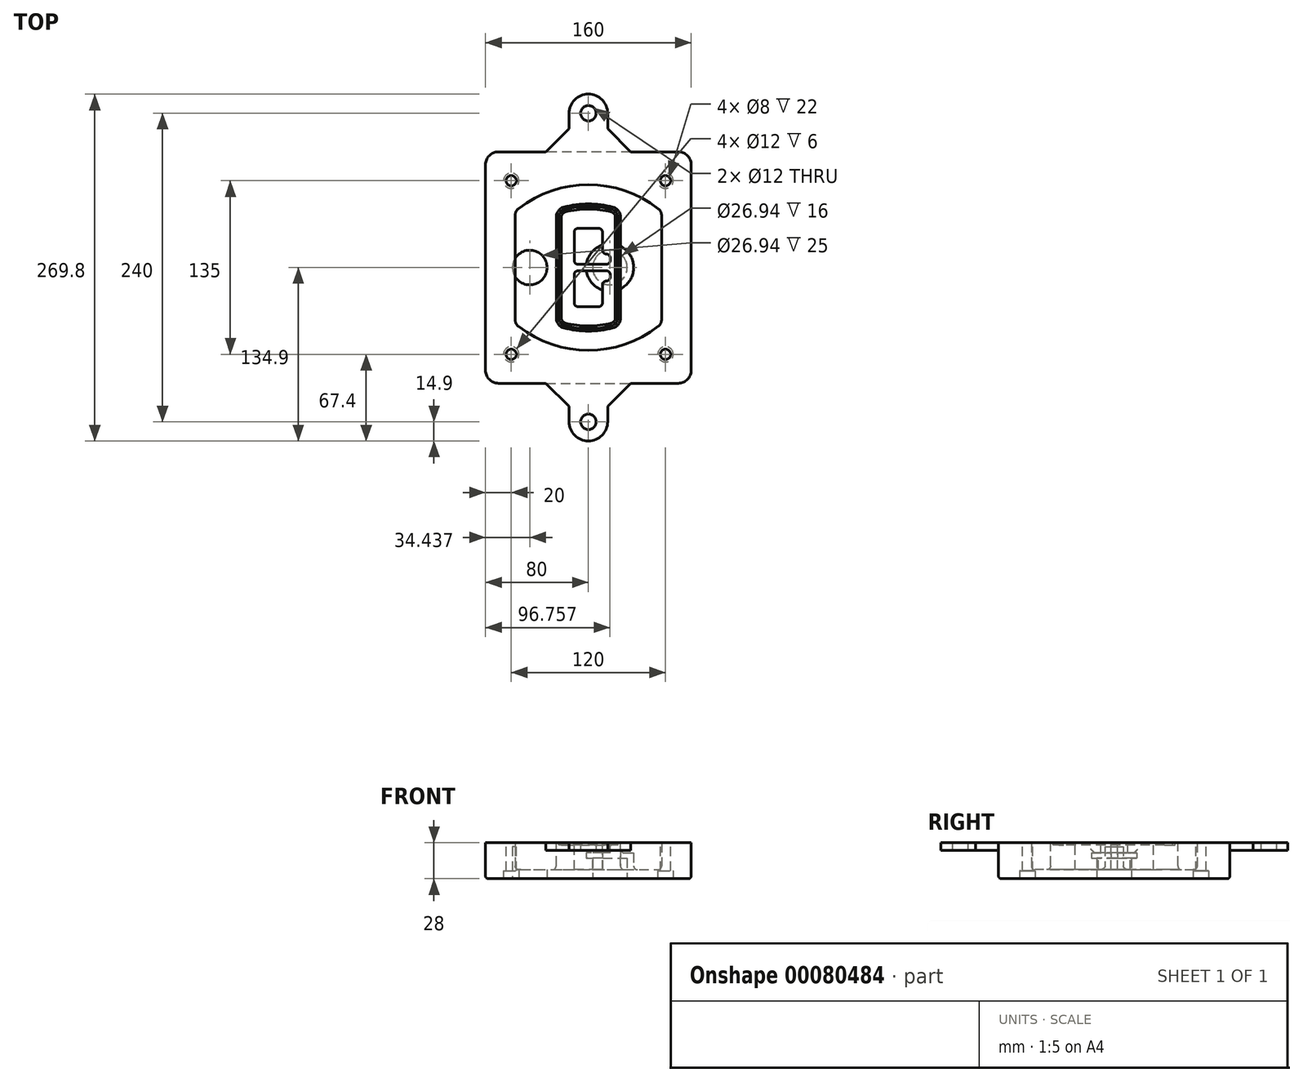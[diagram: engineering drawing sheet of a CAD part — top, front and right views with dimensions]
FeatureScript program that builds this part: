
annotation { "Feature Type Name" : "Feature", "Feature Type Description" : "" }
export const myFeature = defineFeature(function(context is Context, id is Id, definition is map)
    precondition{}
    {
        {
            var Q0;
            Q0=qCreatedBy(makeId("Top.planeOp"),FACE);
            var sketch = newSketch(context, id + "F0", { "sketchPlane" : qUnion([Q0])});
            skPoint(sketch, "E0.rect.middle", {"position": v(0, 0) * mm});
            skLineSegment(sketch, "E1.bottom", {"start": v(-70, -90) * mm, "end": v(70, -90) * mm});
            skLineSegment(sketch, "E1.top", {"start": v(-70, 90) * mm, "end": v(70, 90) * mm});
            skLineSegment(sketch, "E1.left", {"start": v(-80, -80) * mm, "end": v(-80, 80) * mm});
            skLineSegment(sketch, "E1.right", {"start": v(80, -80) * mm, "end": v(80, 80) * mm});
            skLineSegment(sketch, "E2", {"start": v(-80, 90) * mm, "end": v(80, -90) * mm, "construction": true});
            skLineSegment(sketch, "E3", {"start": v(80, 90) * mm, "end": v(-80, -90) * mm, "construction": true});
            skCircle(sketch, "E4", {"center": v(-60, 67.5) * mm, "radius": 4 * mm});
            skCircle(sketch, "E5", {"center": v(60, 67.5) * mm, "radius": 4 * mm});
            skCircle(sketch, "E6", {"center": v(60, -67.5) * mm, "radius": 4 * mm});
            skCircle(sketch, "E7", {"center": v(-60, -67.5) * mm, "radius": 4 * mm});
            skLineSegment(sketch, "E8", {"start": v(-60, 67.5) * mm, "end": v(60, 67.5) * mm, "construction": true});
            skLineSegment(sketch, "E9", {"start": v(60, 67.5) * mm, "end": v(60, -67.5) * mm, "construction": true});
            skLineSegment(sketch, "E10", {"start": v(60, -67.5) * mm, "end": v(-60, -67.5) * mm, "construction": true});
            skLineSegment(sketch, "E11", {"start": v(-60, -67.5) * mm, "end": v(-60, 67.5) * mm, "construction": true});
            skLineSegment(sketch, "E12", {"start": v(-60, 40.3) * mm, "end": v(-60, -40.3) * mm});
            skLineSegment(sketch, "E13", {"start": v(60, 40.3) * mm, "end": v(60, -40.3) * mm});
            skArc(sketch, "E14", {"start": v(56.15, 48.18) * mm, "mid": v(0, 67.5) * mm, "end": v(-56.15, 48.18) * mm});
            skArc(sketch, "E15", {"start": v(-56.15, -48.18) * mm, "mid": v(0, -67.5) * mm, "end": v(56.15, -48.18) * mm});
            skLineSegment(sketch, "E16", {"start": v(-60, 0) * mm, "end": v(60, 0) * mm, "construction": true});
            skPoint(sketch, "E17.visualSharp", {"position": v(-60, -45) * mm});
            skArc(sketch, "E17.filletArc", {"start": v(-60, -40.3) * mm, "mid": v(-58.99, -44.68) * mm, "end": v(-56.15, -48.18) * mm});
            skPoint(sketch, "E18.visualSharp", {"position": v(-60, 45) * mm});
            skArc(sketch, "E18.filletArc", {"start": v(-56.15, 48.18) * mm, "mid": v(-58.99, 44.68) * mm, "end": v(-60, 40.3) * mm});
            skPoint(sketch, "E19.visualSharp", {"position": v(60, 45) * mm});
            skArc(sketch, "E19.filletArc", {"start": v(60, 40.3) * mm, "mid": v(58.99, 44.68) * mm, "end": v(56.15, 48.18) * mm});
            skPoint(sketch, "E20.visualSharp", {"position": v(60, -45) * mm});
            skArc(sketch, "E20.filletArc", {"start": v(56.15, -48.18) * mm, "mid": v(58.99, -44.68) * mm, "end": v(60, -40.3) * mm});
            skPoint(sketch, "E21.visualSharp", {"position": v(-80, 90) * mm});
            skArc(sketch, "E21.filletArc", {"start": v(-70, 90) * mm, "mid": v(-77.07, 87.07) * mm, "end": v(-80, 80) * mm});
            skPoint(sketch, "E22.visualSharp", {"position": v(80, 90) * mm});
            skArc(sketch, "E22.filletArc", {"start": v(80, 80) * mm, "mid": v(77.07, 87.07) * mm, "end": v(70, 90) * mm});
            skPoint(sketch, "E23.visualSharp", {"position": v(80, -90) * mm});
            skArc(sketch, "E23.filletArc", {"start": v(70, -90) * mm, "mid": v(77.07, -87.07) * mm, "end": v(80, -80) * mm});
            skPoint(sketch, "E24.visualSharp", {"position": v(-80, -90) * mm});
            skArc(sketch, "E24.filletArc", {"start": v(-80, -80) * mm, "mid": v(-77.07, -87.07) * mm, "end": v(-70, -90) * mm});
            skArc(sketch, "E25.0", {"start": v(57, 40.3) * mm, "mid": v(56.3, 43.36) * mm, "end": v(54.3, 45.81) * mm});
            skLineSegment(sketch, "E25.1", {"start": v(57, 40.3) * mm, "end": v(57, -40.3) * mm});
            skArc(sketch, "E25.2", {"start": v(54.3, -45.81) * mm, "mid": v(56.3, -43.36) * mm, "end": v(57, -40.3) * mm});
            skArc(sketch, "E25.3", {"start": v(-54.3, -45.81) * mm, "mid": v(0, -64.5) * mm, "end": v(54.3, -45.81) * mm});
            skArc(sketch, "E25.4", {"start": v(-57, -40.3) * mm, "mid": v(-56.3, -43.36) * mm, "end": v(-54.3, -45.81) * mm});
            skArc(sketch, "E25.5", {"start": v(54.3, 45.81) * mm, "mid": v(0, 64.5) * mm, "end": v(-54.3, 45.81) * mm});
            skLineSegment(sketch, "E25.6", {"start": v(-57, 40.3) * mm, "end": v(-57, -40.3) * mm});
            skArc(sketch, "E25.7", {"start": v(-54.3, 45.81) * mm, "mid": v(-56.3, 43.36) * mm, "end": v(-57, 40.3) * mm});
            skArc(sketch, "E26.0", {"start": v(-58.62, 51.33) * mm, "mid": v(-62.58, 46.43) * mm, "end": v(-64, 40.3) * mm});
            skArc(sketch, "E26.1", {"start": v(58.62, 51.33) * mm, "mid": v(0, 71.5) * mm, "end": v(-58.62, 51.33) * mm});
            skArc(sketch, "E26.2", {"start": v(64, 40.3) * mm, "mid": v(62.58, 46.43) * mm, "end": v(58.62, 51.33) * mm});
            skLineSegment(sketch, "E26.3", {"start": v(64, 40.3) * mm, "end": v(64, -40.3) * mm});
            skArc(sketch, "E26.4", {"start": v(58.62, -51.33) * mm, "mid": v(62.58, -46.43) * mm, "end": v(64, -40.3) * mm});
            skLineSegment(sketch, "E26.5", {"start": v(-64, 40.3) * mm, "end": v(-64, -40.3) * mm});
            skArc(sketch, "E26.6", {"start": v(-58.62, -51.33) * mm, "mid": v(0, -71.5) * mm, "end": v(58.62, -51.33) * mm});
            skArc(sketch, "E26.7", {"start": v(-64, -40.3) * mm, "mid": v(-62.58, -46.43) * mm, "end": v(-58.62, -51.33) * mm});
            skSolve(sketch);
        }
        {
            var Q0;
            Q0=makeQuery(id+"F0.imprint","IMPRINT",FACE,{"disambiguationData":[TD([[makeQuery(id+"F0.imprint","IMPRINT",EDGE,{"derivedFrom":sQuery(id+"F0.wireOp",EDGE,"E1.bottom")}),1.0]])]});
            var Q1;
            Q1=makeQuery(id+"F0.imprint","IMPRINT",FACE,{"disambiguationData":[TD([[makeQuery(id+"F0.imprint","IMPRINT",EDGE,{"derivedFrom":sQuery(id+"F0.wireOp",EDGE,"E12")}),1.0]])]});
            var Q2;
            Q2=makeQuery(id+"F0.imprint","IMPRINT",FACE,{"disambiguationData":[TD([[makeQuery(id+"F0.imprint","IMPRINT",EDGE,{"derivedFrom":sQuery(id+"F0.wireOp",EDGE,"E25.0")}),1.0]])]});
            var Q3;
            Q3=makeQuery(id+"F0.imprint","IMPRINT",FACE,{"disambiguationData":[TD([[makeQuery(id+"F0.imprint","IMPRINT",EDGE,{"derivedFrom":sQuery(id+"F0.wireOp",EDGE,"E12")}),-1.0]])]});
            extrude(context, id + "F1", {"entities" : qUnion([Q0, Q1, Q2, Q3]), "oppositeDirection" : true, "depth" : 25 * mm});
        }
        {
            var Q0;
            Q0=makeQuery(id+"F0.imprint","IMPRINT",FACE,{"disambiguationData":[TD([[makeQuery(id+"F0.imprint","IMPRINT",EDGE,{"derivedFrom":sQuery(id+"F0.wireOp",EDGE,"E12")}),1.0]])]});
            extrude(context, id + "F2", {"entities" : qUnion([Q0]), "operationType" : NewBodyOperationType.ADD, "depth" : 3 * mm});
        }
        {
            var Q0;
            Q0=makeQuery(id+"F0.imprint","IMPRINT",FACE,{"disambiguationData":[TD([[makeQuery(id+"F0.imprint","IMPRINT",EDGE,{"derivedFrom":sQuery(id+"F0.wireOp",EDGE,"E25.0")}),1.0]])]});
            extrude(context, id + "F3", {"entities" : qUnion([Q0]), "operationType" : NewBodyOperationType.REMOVE, "oppositeDirection" : true, "depth" : 18 * mm});
        }
        {
            var Q0;
            Q0=makeQuery(id+"F2.opExtrude","CAP_FACE",FACE,{"disambiguationData":[OSD([sQuery(id+"F0.wireOp",EDGE,"E12"),sQuery(id+"F0.wireOp",EDGE,"E13"),sQuery(id+"F0.wireOp",EDGE,"E14"),sQuery(id+"F0.wireOp",EDGE,"E15"),sQuery(id+"F0.wireOp",EDGE,"E17.filletArc"),sQuery(id+"F0.wireOp",EDGE,"E18.filletArc"),sQuery(id+"F0.wireOp",EDGE,"E19.filletArc"),sQuery(id+"F0.wireOp",EDGE,"E20.filletArc"),sQuery(id+"F0.wireOp",EDGE,"E25.0"),sQuery(id+"F0.wireOp",EDGE,"E25.1"),sQuery(id+"F0.wireOp",EDGE,"E25.2"),sQuery(id+"F0.wireOp",EDGE,"E25.3"),sQuery(id+"F0.wireOp",EDGE,"E25.4"),sQuery(id+"F0.wireOp",EDGE,"E25.5"),sQuery(id+"F0.wireOp",EDGE,"E25.6"),sQuery(id+"F0.wireOp",EDGE,"E25.7")])],"isStart":false});
            var sketch = newSketch(context, id + "F4", { "sketchPlane" : qUnion([Q0])});
            skArc(sketch, "E27.0", {"start": v(-19.08, -46.97) * mm, "mid": v(0, -49.5) * mm, "end": v(19.08, -46.97) * mm});
            skArc(sketch, "E28.0", {"start": v(19.08, 46.97) * mm, "mid": v(0, 49.5) * mm, "end": v(-19.08, 46.97) * mm});
            skLineSegment(sketch, "E29", {"start": v(-25, 39.25) * mm, "end": v(-25, -39.25) * mm});
            skLineSegment(sketch, "E30", {"start": v(25, 39.25) * mm, "end": v(25, -39.25) * mm});
            skLineSegment(sketch, "E31", {"start": v(-25, 45.1) * mm, "end": v(25, 45.1) * mm, "construction": true});
            skLineSegment(sketch, "E32", {"start": v(-25, -45.1) * mm, "end": v(25, -45.1) * mm, "construction": true});
            skPoint(sketch, "E33.visualSharp", {"position": v(-25, 45.1) * mm});
            skArc(sketch, "E33.filletArc", {"start": v(-19.08, 46.97) * mm, "mid": v(-23.35, 44.11) * mm, "end": v(-25, 39.25) * mm});
            skPoint(sketch, "E34.visualSharp", {"position": v(25, 45.1) * mm});
            skArc(sketch, "E34.filletArc", {"start": v(25, 39.25) * mm, "mid": v(23.35, 44.11) * mm, "end": v(19.08, 46.97) * mm});
            skPoint(sketch, "E35.visualSharp", {"position": v(25, -45.1) * mm});
            skArc(sketch, "E35.filletArc", {"start": v(19.08, -46.97) * mm, "mid": v(23.35, -44.11) * mm, "end": v(25, -39.25) * mm});
            skPoint(sketch, "E36.visualSharp", {"position": v(-25, -45.1) * mm});
            skArc(sketch, "E36.filletArc", {"start": v(-25, -39.25) * mm, "mid": v(-23.35, -44.11) * mm, "end": v(-19.08, -46.97) * mm});
            skArc(sketch, "E37.0", {"start": v(54.3, 45.81) * mm, "mid": v(0, 64.5) * mm, "end": v(-54.3, 45.81) * mm});
            skArc(sketch, "E37.1", {"start": v(-54.3, 45.81) * mm, "mid": v(-56.3, 43.36) * mm, "end": v(-57, 40.3) * mm});
            skLineSegment(sketch, "E37.2", {"start": v(-57, 40.3) * mm, "end": v(-57, -40.3) * mm});
            skArc(sketch, "E37.3", {"start": v(-57, -40.3) * mm, "mid": v(-56.3, -43.36) * mm, "end": v(-54.3, -45.81) * mm});
            skArc(sketch, "E37.4", {"start": v(-54.3, -45.81) * mm, "mid": v(0, -64.5) * mm, "end": v(54.3, -45.81) * mm});
            skArc(sketch, "E37.5", {"start": v(54.3, -45.81) * mm, "mid": v(56.3, -43.36) * mm, "end": v(57, -40.3) * mm});
            skLineSegment(sketch, "E37.6", {"start": v(57, 40.3) * mm, "end": v(57, -40.3) * mm});
            skArc(sketch, "E37.7", {"start": v(57, 40.3) * mm, "mid": v(56.3, 43.36) * mm, "end": v(54.3, 45.81) * mm});
            skLineSegment(sketch, "E38.0", {"start": v(23, 39.25) * mm, "end": v(23, -39.25) * mm});
            skArc(sketch, "E38.1", {"start": v(18.56, -45.04) * mm, "mid": v(21.76, -42.9) * mm, "end": v(23, -39.25) * mm});
            skArc(sketch, "E38.2", {"start": v(-18.56, -45.04) * mm, "mid": v(0, -47.5) * mm, "end": v(18.56, -45.04) * mm});
            skArc(sketch, "E38.3", {"start": v(-23, -39.25) * mm, "mid": v(-21.76, -42.9) * mm, "end": v(-18.56, -45.04) * mm});
            skLineSegment(sketch, "E38.4", {"start": v(-23, 39.25) * mm, "end": v(-23, -39.25) * mm});
            skArc(sketch, "E38.5", {"start": v(23, 39.25) * mm, "mid": v(21.76, 42.9) * mm, "end": v(18.56, 45.04) * mm});
            skArc(sketch, "E38.6", {"start": v(-18.56, 45.04) * mm, "mid": v(-21.76, 42.9) * mm, "end": v(-23, 39.25) * mm});
            skArc(sketch, "E38.7", {"start": v(18.56, 45.04) * mm, "mid": v(0, 47.5) * mm, "end": v(-18.56, 45.04) * mm});
            skArc(sketch, "E39.0", {"start": v(21, 39.25) * mm, "mid": v(20.18, 41.68) * mm, "end": v(18.04, 43.1) * mm});
            skLineSegment(sketch, "E39.1", {"start": v(21, 39.25) * mm, "end": v(21, -39.25) * mm});
            skArc(sketch, "E39.2", {"start": v(18.04, -43.1) * mm, "mid": v(20.18, -41.68) * mm, "end": v(21, -39.25) * mm});
            skArc(sketch, "E39.3", {"start": v(-18.04, -43.1) * mm, "mid": v(0, -45.5) * mm, "end": v(18.04, -43.1) * mm});
            skArc(sketch, "E39.4", {"start": v(-21, -39.25) * mm, "mid": v(-20.18, -41.68) * mm, "end": v(-18.04, -43.1) * mm});
            skArc(sketch, "E39.5", {"start": v(18.04, 43.1) * mm, "mid": v(0, 45.5) * mm, "end": v(-18.04, 43.1) * mm});
            skLineSegment(sketch, "E39.6", {"start": v(-21, 39.25) * mm, "end": v(-21, -39.25) * mm});
            skArc(sketch, "E39.7", {"start": v(-18.04, 43.1) * mm, "mid": v(-20.18, 41.68) * mm, "end": v(-21, 39.25) * mm});
            skLineSegment(sketch, "E40", {"start": v(-25, 0) * mm, "end": v(25, 0) * mm, "construction": true});
            skLineSegment(sketch, "E41", {"start": v(-11, 5.5) * mm, "end": v(-11, 27.5) * mm});
            skLineSegment(sketch, "E42", {"start": v(-8, 30.5) * mm, "end": v(8, 30.5) * mm});
            skLineSegment(sketch, "E43", {"start": v(11, 27.5) * mm, "end": v(11, 13.5) * mm});
            skLineSegment(sketch, "E44", {"start": v(14, 10.5) * mm, "end": v(14, 10.5) * mm});
            skLineSegment(sketch, "E45", {"start": v(17, 7.5) * mm, "end": v(17, 5.5) * mm});
            skLineSegment(sketch, "E46", {"start": v(14, 2.5) * mm, "end": v(-8, 2.5) * mm});
            skPoint(sketch, "E47.visualSharp", {"position": v(-11, 30.5) * mm});
            skArc(sketch, "E47.filletArc", {"start": v(-8, 30.5) * mm, "mid": v(-10.12, 29.62) * mm, "end": v(-11, 27.5) * mm});
            skPoint(sketch, "E48.visualSharp", {"position": v(11, 30.5) * mm});
            skArc(sketch, "E48.filletArc", {"start": v(11, 27.5) * mm, "mid": v(10.12, 29.62) * mm, "end": v(8, 30.5) * mm});
            skPoint(sketch, "E49.visualSharp", {"position": v(11, 10.5) * mm});
            skArc(sketch, "E49.filletArc", {"start": v(11, 13.5) * mm, "mid": v(11.88, 11.38) * mm, "end": v(14, 10.5) * mm});
            skPoint(sketch, "E50.visualSharp", {"position": v(17, 10.5) * mm});
            skArc(sketch, "E50.filletArc", {"start": v(17, 7.5) * mm, "mid": v(16.12, 9.62) * mm, "end": v(14, 10.5) * mm});
            skPoint(sketch, "E51.visualSharp", {"position": v(17, 2.5) * mm});
            skArc(sketch, "E51.filletArc", {"start": v(14, 2.5) * mm, "mid": v(16.12, 3.38) * mm, "end": v(17, 5.5) * mm});
            skPoint(sketch, "E52.visualSharp", {"position": v(-11, 2.5) * mm});
            skArc(sketch, "E52.filletArc", {"start": v(-11, 5.5) * mm, "mid": v(-10.12, 3.38) * mm, "end": v(-8, 2.5) * mm});
            skLineSegment(sketch, "E53.0.MirrorCS", {"start": v(14, -2.5) * mm, "end": v(-8, -2.5) * mm});
            skArc(sketch, "E54.0.MirrorCS", {"start": v(-11, -5.5) * mm, "mid": v(-10.12, -3.38) * mm, "end": v(-8, -2.5) * mm});
            skLineSegment(sketch, "E55.0.MirrorCS", {"start": v(-11, -5.5) * mm, "end": v(-11, -27.5) * mm});
            skArc(sketch, "E56.0.MirrorCS", {"start": v(-8, -30.5) * mm, "mid": v(-10.12, -29.62) * mm, "end": v(-11, -27.5) * mm});
            skLineSegment(sketch, "E57.0.MirrorCS", {"start": v(-8, -30.5) * mm, "end": v(8, -30.5) * mm});
            skArc(sketch, "E58.0.MirrorCS", {"start": v(11, -27.5) * mm, "mid": v(10.12, -29.62) * mm, "end": v(8, -30.5) * mm});
            skLineSegment(sketch, "E59.0.MirrorCS", {"start": v(11, -27.5) * mm, "end": v(11, -13.5) * mm});
            skArc(sketch, "E60.0.MirrorCS", {"start": v(11, -13.5) * mm, "mid": v(11.88, -11.38) * mm, "end": v(14, -10.5) * mm});
            skArc(sketch, "E61.0.MirrorCS", {"start": v(17, -7.5) * mm, "mid": v(16.12, -9.62) * mm, "end": v(14, -10.5) * mm});
            skLineSegment(sketch, "E62.0.MirrorCS", {"start": v(17, -7.5) * mm, "end": v(17, -5.5) * mm});
            skArc(sketch, "E63.0.MirrorCS", {"start": v(14, -2.5) * mm, "mid": v(16.12, -3.38) * mm, "end": v(17, -5.5) * mm});
            skSolve(sketch);
        }
        {
            var Q0;
            Q0=makeQuery(id+"F4.imprint","IMPRINT",FACE,{"disambiguationData":[TD([[makeQuery(id+"F4.imprint","IMPRINT",EDGE,{"derivedFrom":sQuery(id+"F4.wireOp",EDGE,"E27.0")}),1.0]])]});
            var Q1;
            Q1=makeQuery(id+"F4.imprint","IMPRINT",FACE,{"disambiguationData":[TD([[makeQuery(id+"F4.imprint","IMPRINT",EDGE,{"derivedFrom":sQuery(id+"F4.wireOp",EDGE,"E38.0")}),-1.0]])]});
            var Q2;
            Q2=makeQuery(id+"F4.imprint","IMPRINT",FACE,{"disambiguationData":[TD([[makeQuery(id+"F4.imprint","IMPRINT",EDGE,{"derivedFrom":sQuery(id+"F4.wireOp",EDGE,"E39.0")}),1.0]])]});
            extrude(context, id + "F5", {"entities" : qUnion([Q0, Q1, Q2]), "operationType" : NewBodyOperationType.ADD, "endBound" : BoundingType.UP_TO_NEXT, "oppositeDirection" : true, "depth" : 25 * mm});
        }
        {
            var Q0;
            Q0=makeQuery(id+"F4.imprint","IMPRINT",FACE,{"disambiguationData":[TD([[makeQuery(id+"F4.imprint","IMPRINT",EDGE,{"derivedFrom":sQuery(id+"F4.wireOp",EDGE,"E38.0")}),-1.0]])]});
            extrude(context, id + "F6", {"entities" : qUnion([Q0]), "operationType" : NewBodyOperationType.REMOVE, "oppositeDirection" : true, "depth" : 2 * mm});
        }
        {
            var Q0;
            Q0=makeQuery(id+"F1.opExtrude","CAP_FACE",FACE,{"disambiguationData":[OSD([sQuery(id+"F0.wireOp",EDGE,"E1.bottom"),sQuery(id+"F0.wireOp",EDGE,"E1.top"),sQuery(id+"F0.wireOp",EDGE,"E1.left"),sQuery(id+"F0.wireOp",EDGE,"E1.right"),sQuery(id+"F0.wireOp",EDGE,"E4"),sQuery(id+"F0.wireOp",EDGE,"E5"),sQuery(id+"F0.wireOp",EDGE,"E6"),sQuery(id+"F0.wireOp",EDGE,"E7"),sQuery(id+"F0.wireOp",EDGE,"E21.filletArc"),sQuery(id+"F0.wireOp",EDGE,"E22.filletArc"),sQuery(id+"F0.wireOp",EDGE,"E23.filletArc"),sQuery(id+"F0.wireOp",EDGE,"E24.filletArc")])],"isStart":false});
            var sketch = newSketch(context, id + "F7", { "sketchPlane" : qUnion([Q0])});
            skCircle(sketch, "E64", {"center": v(16.76, 0) * mm, "radius": 13.47 * mm});
            skCircle(sketch, "E65", {"center": v(-45.56, 0) * mm, "radius": 13.47 * mm});
            skLineSegment(sketch, "E66", {"start": v(80, 0) * mm, "end": v(-80, 0) * mm});
            skCircle(sketch, "E67", {"center": v(16.76, 0) * mm, "radius": 18.47 * mm});
            skCircle(sketch, "E68", {"center": v(60, -67.5) * mm, "radius": 6 * mm});
            skCircle(sketch, "E69", {"center": v(-60, -67.5) * mm, "radius": 6 * mm});
            skCircle(sketch, "E70", {"center": v(-60, 67.5) * mm, "radius": 6 * mm});
            skCircle(sketch, "E71", {"center": v(60, 67.5) * mm, "radius": 6 * mm});
            skSolve(sketch);
        }
        {
            var Q0;
            {var subQ1=sQuery(id+"F7.wireOp",EDGE,"E66");var subQ4=sQuery(id+"F7.wireOp",EDGE,"E64");var subQ6=makeQuery(id+"F7.imprint","INTERSECT",VERTEX,{"disambiguationData":[OD(0.0)],"derivedFrom":[subQ4,subQ1]});Q0=makeQuery(id+"F7.imprint","IMPRINT",FACE,{"disambiguationData":[TD([[makeQuery(id+"F7.imprint","IMPRINT",EDGE,{"disambiguationData":[TD([[subQ6,-1.0]])],"derivedFrom":subQ4}),-1.0]])]});}
            var Q1;
            {var subQ0=sQuery(id+"F7.wireOp",EDGE,"E66");var subQ1=sQuery(id+"F7.wireOp",EDGE,"E64");var subQ3=makeQuery(id+"F7.imprint","INTERSECT",VERTEX,{"disambiguationData":[OD(0.0)],"derivedFrom":[subQ1,subQ0]});Q1=makeQuery(id+"F7.imprint","IMPRINT",FACE,{"disambiguationData":[TD([[makeQuery(id+"F7.imprint","IMPRINT",EDGE,{"disambiguationData":[TD([[subQ3,-1.0]])],"derivedFrom":subQ1}),1.0]])]});}
            var Q2;
            {var subQ0=sQuery(id+"F7.wireOp",EDGE,"E66");var subQ1=sQuery(id+"F7.wireOp",EDGE,"E64");var subQ3=makeQuery(id+"F7.imprint","INTERSECT",VERTEX,{"disambiguationData":[OD(0.0)],"derivedFrom":[subQ1,subQ0]});Q2=makeQuery(id+"F7.imprint","IMPRINT",FACE,{"disambiguationData":[TD([[makeQuery(id+"F7.imprint","IMPRINT",EDGE,{"disambiguationData":[TD([[subQ3,1.0]])],"derivedFrom":subQ1}),1.0]])]});}
            var Q3;
            {var subQ1=sQuery(id+"F7.wireOp",EDGE,"E66");var subQ4=sQuery(id+"F7.wireOp",EDGE,"E64");var subQ6=makeQuery(id+"F7.imprint","INTERSECT",VERTEX,{"disambiguationData":[OD(0.0)],"derivedFrom":[subQ4,subQ1]});Q3=makeQuery(id+"F7.imprint","IMPRINT",FACE,{"disambiguationData":[TD([[makeQuery(id+"F7.imprint","IMPRINT",EDGE,{"disambiguationData":[TD([[subQ6,1.0]])],"derivedFrom":subQ4}),-1.0]])]});}
            extrude(context, id + "F8", {"entities" : qUnion([Q0, Q1, Q2, Q3]), "operationType" : NewBodyOperationType.ADD, "oppositeDirection" : true, "depth" : 20 * mm});
        }
        {
            var Q0;
            {var subQ0=sQuery(id+"F7.wireOp",EDGE,"E66");var subQ1=sQuery(id+"F7.wireOp",EDGE,"E64");var subQ3=makeQuery(id+"F7.imprint","INTERSECT",VERTEX,{"disambiguationData":[OD(0.0)],"derivedFrom":[subQ1,subQ0]});Q0=makeQuery(id+"F7.imprint","IMPRINT",FACE,{"disambiguationData":[TD([[makeQuery(id+"F7.imprint","IMPRINT",EDGE,{"disambiguationData":[TD([[subQ3,-1.0]])],"derivedFrom":subQ1}),1.0]])]});}
            var Q1;
            {var subQ0=sQuery(id+"F7.wireOp",EDGE,"E66");var subQ1=sQuery(id+"F7.wireOp",EDGE,"E64");var subQ3=makeQuery(id+"F7.imprint","INTERSECT",VERTEX,{"disambiguationData":[OD(0.0)],"derivedFrom":[subQ1,subQ0]});Q1=makeQuery(id+"F7.imprint","IMPRINT",FACE,{"disambiguationData":[TD([[makeQuery(id+"F7.imprint","IMPRINT",EDGE,{"disambiguationData":[TD([[subQ3,1.0]])],"derivedFrom":subQ1}),1.0]])]});}
            extrude(context, id + "F9", {"entities" : qUnion([Q0, Q1]), "operationType" : NewBodyOperationType.REMOVE, "oppositeDirection" : true, "depth" : 16 * mm});
        }
        {
            var Q0;
            {var subQ0=sQuery(id+"F7.wireOp",EDGE,"E66");var subQ1=sQuery(id+"F7.wireOp",EDGE,"E65");var subQ3=makeQuery(id+"F7.imprint","INTERSECT",VERTEX,{"disambiguationData":[OD(0.0)],"derivedFrom":[subQ1,subQ0]});Q0=makeQuery(id+"F7.imprint","IMPRINT",FACE,{"disambiguationData":[TD([[makeQuery(id+"F7.imprint","IMPRINT",EDGE,{"disambiguationData":[TD([[subQ3,-1.0]])],"derivedFrom":subQ1}),1.0]])]});}
            var Q1;
            {var subQ0=sQuery(id+"F7.wireOp",EDGE,"E66");var subQ1=sQuery(id+"F7.wireOp",EDGE,"E65");var subQ3=makeQuery(id+"F7.imprint","INTERSECT",VERTEX,{"disambiguationData":[OD(0.0)],"derivedFrom":[subQ1,subQ0]});Q1=makeQuery(id+"F7.imprint","IMPRINT",FACE,{"disambiguationData":[TD([[makeQuery(id+"F7.imprint","IMPRINT",EDGE,{"disambiguationData":[TD([[subQ3,1.0]])],"derivedFrom":subQ1}),1.0]])]});}
            extrude(context, id + "F10", {"entities" : qUnion([Q0, Q1]), "operationType" : NewBodyOperationType.REMOVE, "oppositeDirection" : true, "depth" : 25 * mm});
        }
        {
            var Q0;
            Q0=makeQuery(id+"F7.imprint","IMPRINT",FACE,{"disambiguationData":[TD([[makeQuery(id+"F7.imprint","IMPRINT",EDGE,{"derivedFrom":sQuery(id+"F7.wireOp",EDGE,"E68")}),1.0]])]});
            var Q1;
            Q1=makeQuery(id+"F7.imprint","IMPRINT",FACE,{"disambiguationData":[TD([[makeQuery(id+"F7.imprint","IMPRINT",EDGE,{"derivedFrom":makeQuery(id+"F1.opExtrude","CAP_EDGE",EDGE,{"disambiguationData":[OSD([sQuery(id+"F0.wireOp",EDGE,"E5")])],"isStart":false})}),-1.0]])]});
            var Q2;
            Q2=makeQuery(id+"F7.imprint","IMPRINT",FACE,{"disambiguationData":[TD([[makeQuery(id+"F7.imprint","IMPRINT",EDGE,{"derivedFrom":sQuery(id+"F7.wireOp",EDGE,"E69")}),1.0]])]});
            var Q3;
            Q3=makeQuery(id+"F7.imprint","IMPRINT",FACE,{"disambiguationData":[TD([[makeQuery(id+"F7.imprint","IMPRINT",EDGE,{"derivedFrom":makeQuery(id+"F1.opExtrude","CAP_EDGE",EDGE,{"disambiguationData":[OSD([sQuery(id+"F0.wireOp",EDGE,"E4")])],"isStart":false})}),-1.0]])]});
            var Q4;
            Q4=makeQuery(id+"F7.imprint","IMPRINT",FACE,{"disambiguationData":[TD([[makeQuery(id+"F7.imprint","IMPRINT",EDGE,{"derivedFrom":sQuery(id+"F7.wireOp",EDGE,"E70")}),1.0]])]});
            var Q5;
            Q5=makeQuery(id+"F7.imprint","IMPRINT",FACE,{"disambiguationData":[TD([[makeQuery(id+"F7.imprint","IMPRINT",EDGE,{"derivedFrom":makeQuery(id+"F1.opExtrude","CAP_EDGE",EDGE,{"disambiguationData":[OSD([sQuery(id+"F0.wireOp",EDGE,"E7")])],"isStart":false})}),-1.0]])]});
            var Q6;
            Q6=makeQuery(id+"F7.imprint","IMPRINT",FACE,{"disambiguationData":[TD([[makeQuery(id+"F7.imprint","IMPRINT",EDGE,{"derivedFrom":sQuery(id+"F7.wireOp",EDGE,"E71")}),1.0]])]});
            var Q7;
            Q7=makeQuery(id+"F7.imprint","IMPRINT",FACE,{"disambiguationData":[TD([[makeQuery(id+"F7.imprint","IMPRINT",EDGE,{"derivedFrom":makeQuery(id+"F1.opExtrude","CAP_EDGE",EDGE,{"disambiguationData":[OSD([sQuery(id+"F0.wireOp",EDGE,"E6")])],"isStart":false})}),-1.0]])]});
            extrude(context, id + "F11", {"entities" : qUnion([Q0, Q1, Q2, Q3, Q4, Q5, Q6, Q7]), "operationType" : NewBodyOperationType.REMOVE, "oppositeDirection" : true, "depth" : 6 * mm});
        }
        {
            var Q0;
            Q0=makeQuery(id+"F9.boolean.opBoolean","COPY",FACE,{"derivedFrom":makeQuery(id+"F9.opExtrude","CAP_FACE",FACE,{"disambiguationData":[OSD([sQuery(id+"F7.wireOp",EDGE,"E64")])],"isStart":false})});
            var sketch = newSketch(context, id + "F12", { "sketchPlane" : qUnion([Q0])});
            skArc(sketch, "E72.0", {"start": v(11, 17.55) * mm, "mid": v(2.57, 11.82) * mm, "end": v(-1.54, 2.5) * mm});
            skArc(sketch, "E72.1", {"start": v(-1.54, -2.5) * mm, "mid": v(2.57, -11.82) * mm, "end": v(11, -17.55) * mm});
            skLineSegment(sketch, "E73", {"start": v(-1.54, -2.5) * mm, "end": v(14, -2.5) * mm});
            skLineSegment(sketch, "E74.0", {"start": v(14, 2.5) * mm, "end": v(-1.54, 2.5) * mm});
            skArc(sketch, "E74.1", {"start": v(14, 2.5) * mm, "mid": v(16.12, 3.38) * mm, "end": v(17, 5.5) * mm});
            skLineSegment(sketch, "E74.2", {"start": v(17, 7.5) * mm, "end": v(17, 5.5) * mm});
            skArc(sketch, "E74.3", {"start": v(17, 7.5) * mm, "mid": v(16.12, 9.62) * mm, "end": v(14, 10.5) * mm});
            skArc(sketch, "E74.4", {"start": v(11, 13.5) * mm, "mid": v(11.88, 11.38) * mm, "end": v(14, 10.5) * mm});
            skLineSegment(sketch, "E74.5", {"start": v(11, 17.55) * mm, "end": v(11, 13.5) * mm});
            skLineSegment(sketch, "E74.7", {"start": v(14, -2.5) * mm, "end": v(-1.54, -2.5) * mm});
            skArc(sketch, "E74.8", {"start": v(14, -2.5) * mm, "mid": v(16.12, -3.38) * mm, "end": v(17, -5.5) * mm});
            skLineSegment(sketch, "E74.9", {"start": v(17, -7.5) * mm, "end": v(17, -5.5) * mm});
            skArc(sketch, "E74.10", {"start": v(17, -7.5) * mm, "mid": v(16.12, -9.62) * mm, "end": v(14, -10.5) * mm});
            skArc(sketch, "E74.11", {"start": v(11, -13.5) * mm, "mid": v(11.88, -11.38) * mm, "end": v(14, -10.5) * mm});
            skLineSegment(sketch, "E74.12", {"start": v(11, -17.55) * mm, "end": v(11, -13.5) * mm});
            skPoint(sketch, "E75.orphan", {"position": v(11, -27.5) * mm});
            skPoint(sketch, "E76.orphan", {"position": v(-8, -2.5) * mm});
            skPoint(sketch, "E77.orphan", {"position": v(-8, 2.5) * mm});
            skPoint(sketch, "E78.orphan", {"position": v(11, 27.5) * mm});
            skSolve(sketch);
        }
        {
            var Q0;
            {var subQ7=sQuery(id+"F12.wireOp",EDGE,"E72.0");var subQ14=sQuery(id+"F12.wireOp",EDGE,"E72.1");var subQ16=sQuery(id+"F12.wireOp",EDGE,"E74.1");var subQ18=sQuery(id+"F12.wireOp",EDGE,"E74.8");Q0=qUnion([makeQuery(id+"F12.imprint","IMPRINT",FACE,{"disambiguationData":[TD([[makeQuery(id+"F12.imprint","IMPRINT",EDGE,{"derivedFrom":subQ7}),1.0]])]}),makeQuery(id+"F12.imprint","IMPRINT",FACE,{"disambiguationData":[TD([[makeQuery(id+"F12.imprint","IMPRINT",EDGE,{"derivedFrom":subQ14}),1.0]])]}),makeQuery(id+"F12.imprint","IMPRINT",FACE,{"disambiguationData":[TD([[makeQuery(id+"F12.imprint","IMPRINT",EDGE,{"derivedFrom":subQ16}),1.0]])]}),makeQuery(id+"F12.imprint","IMPRINT",FACE,{"disambiguationData":[TD([[makeQuery(id+"F12.imprint","IMPRINT",EDGE,{"derivedFrom":subQ18}),-1.0]])]})]);}
            var Q1;
            Q1=makeQuery(id+"F5.boolean.opBoolean","SPLIT",FACE,{"disambiguationData":[TD([makeQuery(id+"F5.opExtrude","SWEPT_FACE",FACE,{"disambiguationData":[OSD([sQuery(id+"F4.wireOp",EDGE,"E41")])]})])],"derivedFrom":makeQuery(id+"F3.boolean.opBoolean","COPY",FACE,{"derivedFrom":makeQuery(id+"F3.opExtrude","CAP_FACE",FACE,{"disambiguationData":[OSD([sQuery(id+"F0.wireOp",EDGE,"E25.0"),sQuery(id+"F0.wireOp",EDGE,"E25.1"),sQuery(id+"F0.wireOp",EDGE,"E25.2"),sQuery(id+"F0.wireOp",EDGE,"E25.3"),sQuery(id+"F0.wireOp",EDGE,"E25.4"),sQuery(id+"F0.wireOp",EDGE,"E25.5"),sQuery(id+"F0.wireOp",EDGE,"E25.6"),sQuery(id+"F0.wireOp",EDGE,"E25.7")])],"isStart":false})})});
            extrude(context, id + "F13", {"entities" : qUnion([Q0]), "operationType" : NewBodyOperationType.REMOVE, "endBound" : BoundingType.UP_TO_SURFACE, "endBoundEntityFace" : qUnion([Q1]), "depth" : 25 * mm});
        }
        {
            var Q0;
            Q0=makeQuery(id+"F3.boolean.opBoolean","COPY",EDGE,{"derivedFrom":makeQuery(id+"F3.opExtrude","CAP_EDGE",EDGE,{"disambiguationData":[OSD([sQuery(id+"F0.wireOp",EDGE,"E25.6")])],"isStart":false})});
            var Q1;
            Q1=makeQuery(id+"F8.boolean.opBoolean","INTERSECT",EDGE,{"derivedFrom":[makeQuery(id+"F5.opExtrude","SWEPT_FACE",FACE,{"disambiguationData":[OSD([sQuery(id+"F4.wireOp",EDGE,"E30")])]}),makeQuery(id+"F8.opExtrude","CAP_FACE",FACE,{"disambiguationData":[OSD([sQuery(id+"F7.wireOp",EDGE,"E67")])],"isStart":false})]});
            var Q2;
            Q2=makeQuery(id+"F8.boolean.opBoolean","INTERSECT",EDGE,{"disambiguationData":[OD(1.0)],"derivedFrom":[makeQuery(id+"F5.opExtrude","SWEPT_FACE",FACE,{"disambiguationData":[OSD([sQuery(id+"F4.wireOp",EDGE,"E30")])]}),makeQuery(id+"F8.opExtrude","SWEPT_FACE",FACE,{"disambiguationData":[OSD([sQuery(id+"F7.wireOp",EDGE,"E67")])]})]});
            var Q3;
            {var subQ0=sQuery(id+"F4.wireOp",EDGE,"E30");Q3=makeQuery(id+"F8.boolean.opBoolean","SPLIT",EDGE,{"disambiguationData":[TD([makeQuery(id+"F5.opExtrude","SWEPT_FACE",FACE,{"disambiguationData":[OSD([sQuery(id+"F4.wireOp",EDGE,"E35.filletArc")])]})])],"derivedFrom":makeQuery(id+"F5.opExtrude","CAP_EDGE",EDGE,{"disambiguationData":[OSD([subQ0])],"isStart":false})});}
            var Q4;
            {var subQ0=sQuery(id+"F0.wireOp",EDGE,"E25.7");var subQ1=sQuery(id+"F0.wireOp",EDGE,"E25.1");var subQ2=sQuery(id+"F0.wireOp",EDGE,"E25.6");var subQ3=sQuery(id+"F0.wireOp",EDGE,"E25.5");var subQ4=sQuery(id+"F0.wireOp",EDGE,"E25.4");var subQ5=sQuery(id+"F0.wireOp",EDGE,"E25.0");var subQ6=sQuery(id+"F0.wireOp",EDGE,"E25.2");var subQ7=sQuery(id+"F0.wireOp",EDGE,"E25.3");Q4=makeQuery(id+"F8.boolean.opBoolean","INTERSECT",EDGE,{"derivedFrom":[makeQuery(id+"F5.boolean.opBoolean","SPLIT",FACE,{"disambiguationData":[TD([makeQuery(id+"F2.opExtrude","SWEPT_FACE",FACE,{"disambiguationData":[OSD([subQ5])]})])],"derivedFrom":makeQuery(id+"F3.boolean.opBoolean","COPY",FACE,{"derivedFrom":makeQuery(id+"F3.opExtrude","CAP_FACE",FACE,{"disambiguationData":[OSD([subQ5,subQ1,subQ6,subQ7,subQ4,subQ3,subQ2,subQ0])],"isStart":false})})}),makeQuery(id+"F8.opExtrude","SWEPT_FACE",FACE,{"disambiguationData":[OSD([sQuery(id+"F7.wireOp",EDGE,"E67")])]})]});}
            var Q5;
            Q5=makeQuery(id+"F8.boolean.opBoolean","INTERSECT",EDGE,{"disambiguationData":[OD(0.0)],"derivedFrom":[makeQuery(id+"F5.opExtrude","SWEPT_FACE",FACE,{"disambiguationData":[OSD([sQuery(id+"F4.wireOp",EDGE,"E30")])]}),makeQuery(id+"F8.opExtrude","SWEPT_FACE",FACE,{"disambiguationData":[OSD([sQuery(id+"F7.wireOp",EDGE,"E67")])]})]});
            fillet(context, id + "F14", {"entities" : qUnion([Q0, Q1, Q2, Q3, Q4, Q5]), "radius" : 3 * mm, "tangentPropagation" : true, "allowEdgeOverflow" : false});
        }
        {
            var Q0;
            Q0=makeQuery(id+"F1.opExtrude","CAP_EDGE",EDGE,{"disambiguationData":[OSD([sQuery(id+"F0.wireOp",EDGE,"E1.bottom")])],"isStart":false});
            fillet(context, id + "F15", {"entities" : qUnion([Q0]), "radius" : 2 * mm, "tangentPropagation" : true, "allowEdgeOverflow" : false});
        }
        {
            var Q0;
            {var subQ0=sQuery(id+"F0.wireOp",EDGE,"E22.filletArc");var subQ1=sQuery(id+"F0.wireOp",EDGE,"E7");var subQ2=sQuery(id+"F0.wireOp",EDGE,"E6");var subQ3=sQuery(id+"F0.wireOp",EDGE,"E5");var subQ4=sQuery(id+"F0.wireOp",EDGE,"E4");var subQ5=sQuery(id+"F0.wireOp",EDGE,"E1.bottom");var subQ6=sQuery(id+"F0.wireOp",EDGE,"E21.filletArc");var subQ7=sQuery(id+"F0.wireOp",EDGE,"E1.top");var subQ8=sQuery(id+"F0.wireOp",EDGE,"E1.left");var subQ9=sQuery(id+"F0.wireOp",EDGE,"E1.right");var subQ10=sQuery(id+"F0.wireOp",EDGE,"E23.filletArc");var subQ11=sQuery(id+"F0.wireOp",EDGE,"E24.filletArc");Q0=makeQuery(id+"F2.boolean.opBoolean","SPLIT",FACE,{"disambiguationData":[TD([makeQuery(id+"F1.opExtrude","SWEPT_FACE",FACE,{"disambiguationData":[OSD([subQ5])]})])],"derivedFrom":makeQuery(id+"F1.opExtrude","CAP_FACE",FACE,{"disambiguationData":[OSD([subQ5,subQ7,subQ8,subQ9,subQ4,subQ3,subQ2,subQ1,subQ6,subQ0,subQ10,subQ11])],"isStart":true})});}
            var sketch = newSketch(context, id + "F16", { "sketchPlane" : qUnion([Q0])});
            skLineSegment(sketch, "E79", {"start": v(0, 90) * mm, "end": v(0, 120) * mm, "construction": true});
            skCircle(sketch, "E80", {"center": v(0, 120) * mm, "radius": 6 * mm});
            skArc(sketch, "E81", {"start": v(15, 119.9) * mm, "mid": v(0, 134.9) * mm, "end": v(-15, 119.9) * mm});
            skLineSegment(sketch, "E82", {"start": v(-15, 119.9) * mm, "end": v(-15, 108) * mm});
            skLineSegment(sketch, "E83", {"start": v(15, 119.9) * mm, "end": v(15, 108) * mm});
            skLineSegment(sketch, "E84", {"start": v(-15, 108) * mm, "end": v(-33, 90) * mm});
            skLineSegment(sketch, "E85", {"start": v(15, 108) * mm, "end": v(33, 90) * mm});
            skLineSegment(sketch, "E86", {"start": v(-33, 90) * mm, "end": v(33, 90) * mm});
            skLineSegment(sketch, "E87", {"start": v(80, 0) * mm, "end": v(-80, 0) * mm, "construction": true});
            skLineSegment(sketch, "E88.MirrorCS", {"start": v(0, -90) * mm, "end": v(0, -120) * mm, "construction": true});
            skLineSegment(sketch, "E89.MirrorCS", {"start": v(-15, -108) * mm, "end": v(-33, -90) * mm});
            skLineSegment(sketch, "E90.MirrorCS", {"start": v(15, -108) * mm, "end": v(33, -90) * mm});
            skLineSegment(sketch, "E91.MirrorCS", {"start": v(-33, -90) * mm, "end": v(33, -90) * mm});
            skLineSegment(sketch, "E92.MirrorCS", {"start": v(-15, -119.9) * mm, "end": v(-15, -108) * mm});
            skLineSegment(sketch, "E93.MirrorCS", {"start": v(15, -119.9) * mm, "end": v(15, -108) * mm});
            skArc(sketch, "E94.MirrorCS", {"start": v(15, -119.9) * mm, "mid": v(0, -134.9) * mm, "end": v(-15, -119.9) * mm});
            skCircle(sketch, "E95.MirrorC", {"center": v(0, -120) * mm, "radius": 6 * mm});
            skSolve(sketch);
        }
        {
            var Q0;
            Q0=makeQuery(id+"F16.imprint","IMPRINT",FACE,{"disambiguationData":[TD([[makeQuery(id+"F16.imprint","IMPRINT",EDGE,{"derivedFrom":sQuery(id+"F16.wireOp",EDGE,"E80")}),-1.0]])]});
            var Q1;
            {var subQ4=sQuery(id+"F16.wireOp",EDGE,"E86");Q1=makeQuery(id+"F16.imprint","IMPRINT",FACE,{"disambiguationData":[TD([[makeQuery(id+"F16.imprint","IMPRINT",EDGE,{"derivedFrom":subQ4}),-1.0]])]});}
            var Q2;
            Q2=makeQuery(id+"F16.imprint","IMPRINT",FACE,{"disambiguationData":[TD([[makeQuery(id+"F16.imprint","IMPRINT",EDGE,{"derivedFrom":sQuery(id+"F16.wireOp",EDGE,"E89.MirrorCS")}),-1.0]])]});
            extrude(context, id + "F17", {"entities" : qUnion([Q0, Q1, Q2]), "operationType" : NewBodyOperationType.ADD, "endBound" : BoundingType.SYMMETRIC, "depth" : 6 * mm});
        }
    });
